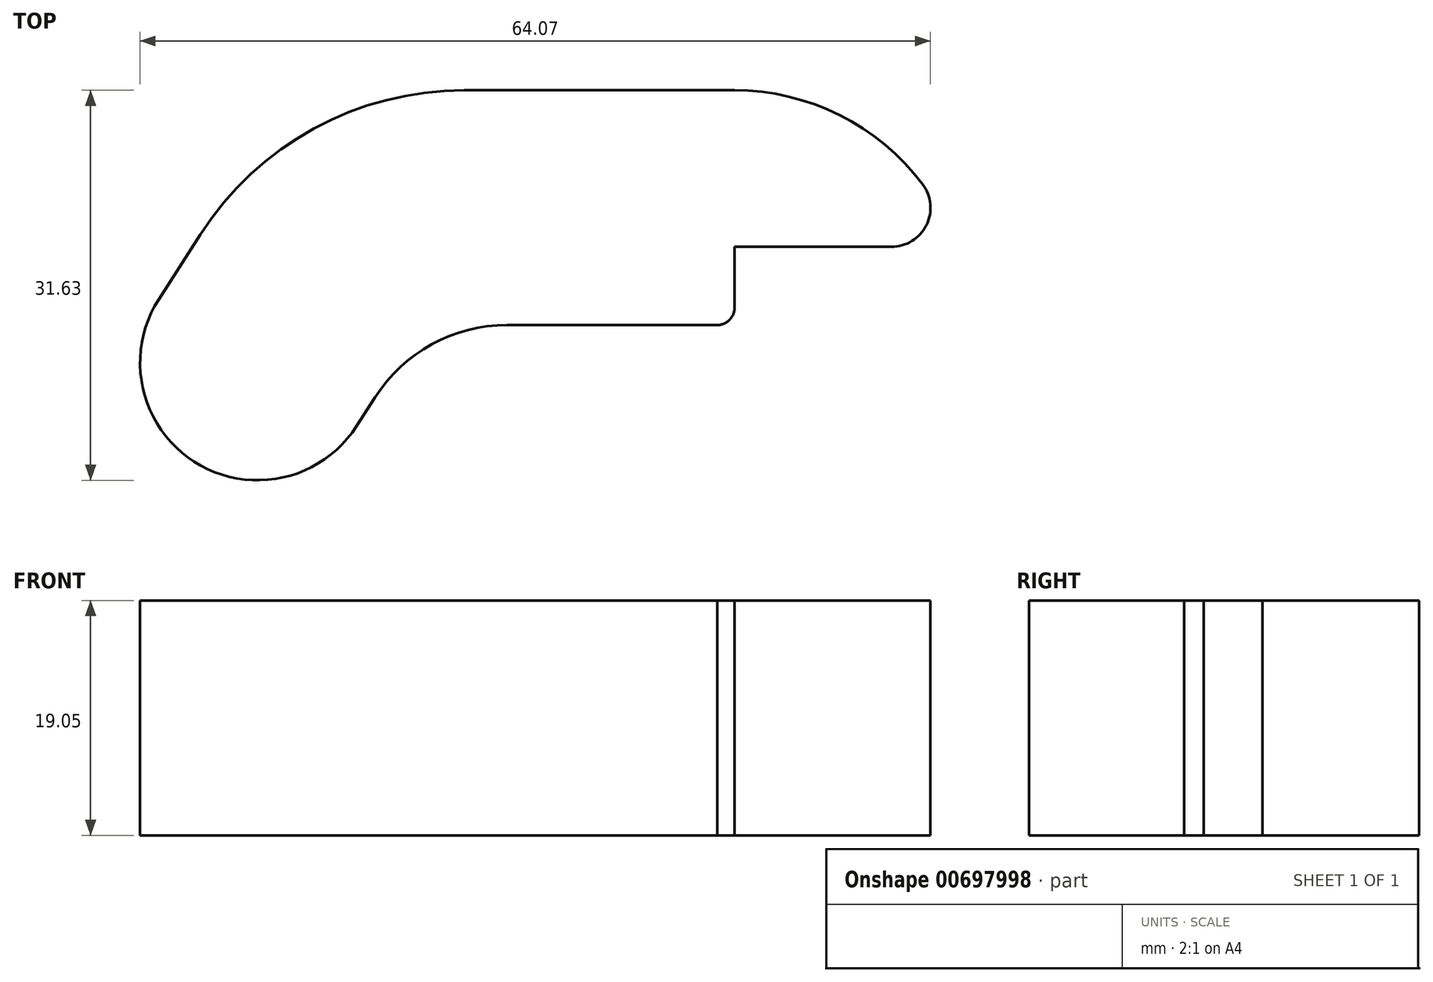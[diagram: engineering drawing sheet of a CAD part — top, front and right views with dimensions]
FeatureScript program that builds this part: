
annotation { "Feature Type Name" : "Feature", "Feature Type Description" : "" }
export const myFeature = defineFeature(function(context is Context, id is Id, definition is map)
    precondition{}
    {
        {
            var Q0;
            Q0=qCreatedBy(makeId("Top.planeOp"),FACE);
            var sketch = newSketch(context, id + "F0", { "sketchPlane" : qUnion([Q0])});
            skLineSegment(sketch, "E0", {"start": v(9.47, 14.78) * mm, "end": v(12.84, 20.05) * mm});
            skLineSegment(sketch, "E1", {"start": v(34.23, 31.75) * mm, "end": v(56.16, 31.75) * mm});
            skLineSegment(sketch, "E2", {"start": v(27.01, 6.85) * mm, "end": v(25.51, 4.5) * mm});
            skArc(sketch, "E3.filletArc", {"start": v(34.23, 31.75) * mm, "mid": v(22.04, 28.63) * mm, "end": v(12.84, 20.05) * mm});
            skArc(sketch, "E4.filletArc", {"start": v(71.4, 24.13) * mm, "mid": v(64.68, 29.74) * mm, "end": v(56.16, 31.75) * mm});
            skArc(sketch, "E5", {"start": v(9.47, 14.78) * mm, "mid": v(12.35, 1.62) * mm, "end": v(25.51, 4.5) * mm});
            skArc(sketch, "E6.filletArc", {"start": v(37.7, 12.7) * mm, "mid": v(31.61, 11.14) * mm, "end": v(27.01, 6.85) * mm});
            skPoint(sketch, "E7.orphan", {"position": v(25.51, 4.5) * mm});
            skPoint(sketch, "E8.start.orphan", {"position": v(9.47, 14.78) * mm});
            skArc(sketch, "E9.filletArc", {"start": v(68.86, 19.05) * mm, "mid": v(71.7, 20.8) * mm, "end": v(71.4, 24.13) * mm});
            skLineSegment(sketch, "E10", {"start": v(68.86, 19.05) * mm, "end": v(56.16, 19.05) * mm});
            skLineSegment(sketch, "E11", {"start": v(56.16, 19.05) * mm, "end": v(56.16, 14.02) * mm});
            skLineSegment(sketch, "E12", {"start": v(37.7, 12.7) * mm, "end": v(54.75, 12.7) * mm});
            skArc(sketch, "E13", {"start": v(54.75, 12.7) * mm, "mid": v(55.8, 13.19) * mm, "end": v(56.16, 14.3) * mm});
            skSolve(sketch);
        }
        {
            var Q0;
            Q0 = qSketchRegion(id + "F0", true);
            extrude(context, id + "F1", {"entities" : qUnion([Q0]), "depth" : 19.05 * mm, "offsetDistance" : 25.4 * mm});
        }
    });
